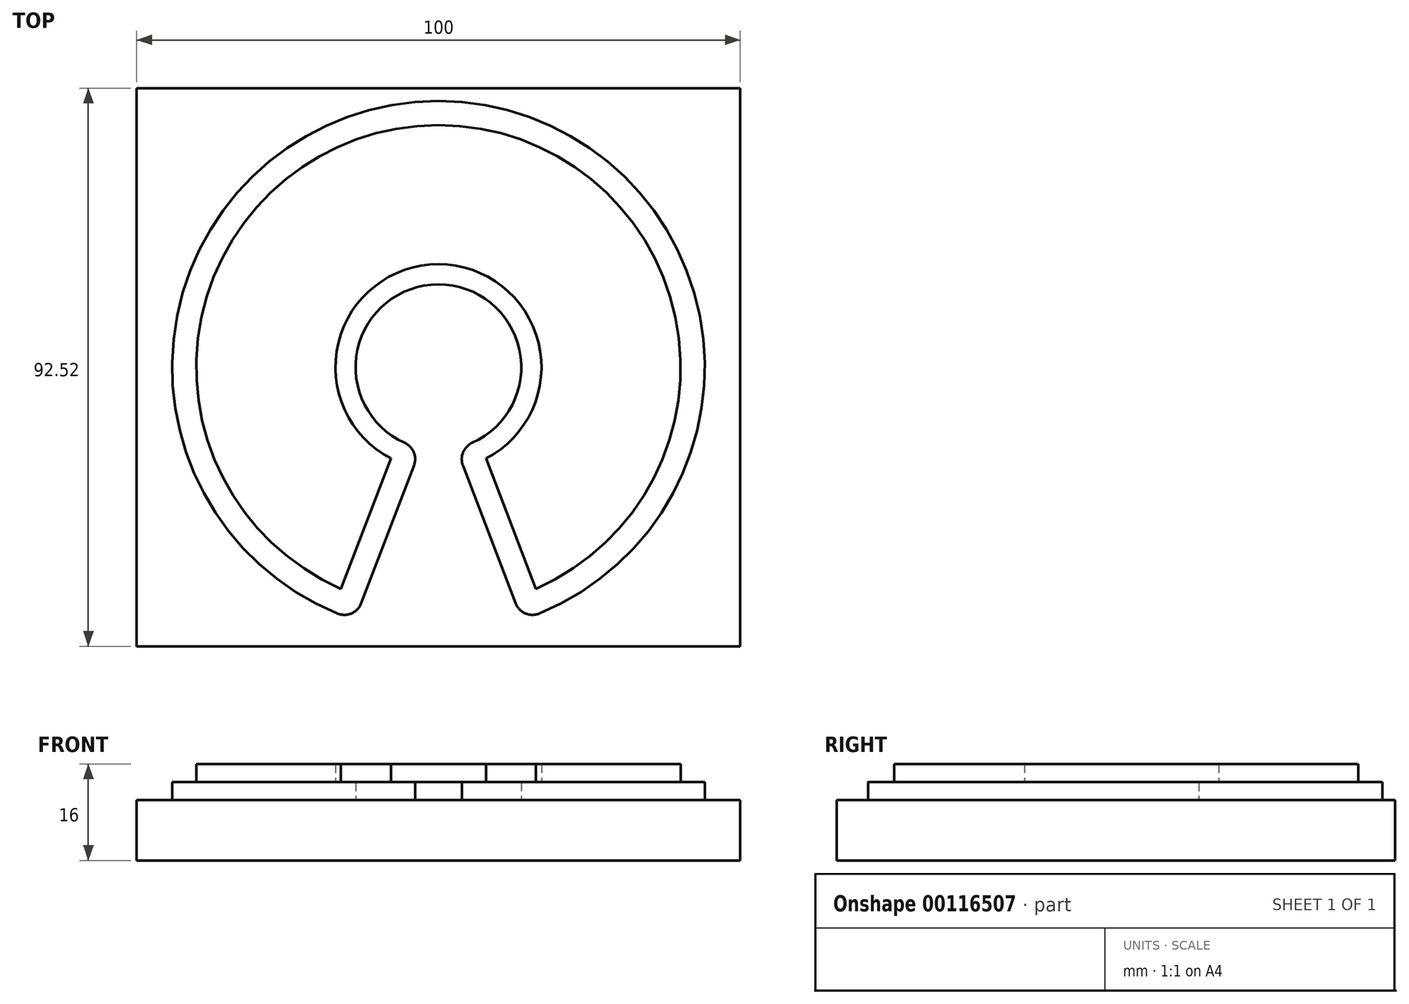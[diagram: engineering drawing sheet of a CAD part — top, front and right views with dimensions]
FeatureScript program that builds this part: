
annotation { "Feature Type Name" : "Feature", "Feature Type Description" : "" }
export const myFeature = defineFeature(function(context is Context, id is Id, definition is map)
    precondition{}
    {
        {
            var Q0;
            Q0=qCreatedBy(makeId("Top.planeOp"),FACE);
            var sketch = newSketch(context, id + "F0", { "sketchPlane" : qUnion([Q0])});
            skLineSegment(sketch, "E0.bottom", {"start": v(50, 46.26) * mm, "end": v(-50, 46.26) * mm});
            skLineSegment(sketch, "E0.top", {"start": v(50, -46.26) * mm, "end": v(-50, -46.26) * mm});
            skLineSegment(sketch, "E0.left", {"start": v(50, 46.26) * mm, "end": v(50, -46.26) * mm});
            skLineSegment(sketch, "E0.right", {"start": v(-50, 46.26) * mm, "end": v(-50, -46.26) * mm});
            skPoint(sketch, "E0.middle", {"position": v(0, 0) * mm});
            skArc(sketch, "E1", {"start": v(16.16, -36.73) * mm, "mid": v(0, 40.13) * mm, "end": v(-16.16, -36.73) * mm});
            skArc(sketch, "E2.0", {"start": v(13.85, -41.9) * mm, "mid": v(0, 44.13) * mm, "end": v(-13.85, -41.9) * mm});
            skArc(sketch, "E3", {"start": v(2.94, -13.41) * mm, "mid": v(0, 13.73) * mm, "end": v(-2.94, -13.41) * mm});
            skLineSegment(sketch, "E4", {"start": v(-7.88, -15.14) * mm, "end": v(-16.16, -36.73) * mm});
            skLineSegment(sketch, "E5.0", {"start": v(-2.94, -13.41) * mm, "end": v(-13.85, -41.9) * mm});
            skLineSegment(sketch, "E6", {"start": v(0, 0) * mm, "end": v(0, -52.2) * mm, "construction": true});
            skLineSegment(sketch, "E7.MirrorCS", {"start": v(7.88, -15.14) * mm, "end": v(16.16, -36.73) * mm});
            skLineSegment(sketch, "E8.MirrorCS", {"start": v(2.94, -13.41) * mm, "end": v(13.85, -41.9) * mm});
            skPoint(sketch, "E9.orphan", {"position": v(1.18, -8.84) * mm});
            skPoint(sketch, "E10.orphan", {"position": v(4.9, -7.35) * mm});
            skPoint(sketch, "E11.orphan", {"position": v(-1.18, -8.84) * mm});
            skPoint(sketch, "E12.orphan", {"position": v(-4.9, -7.35) * mm});
            skArc(sketch, "E13.trimOffspring", {"start": v(7.88, -15.14) * mm, "mid": v(0, 17.07) * mm, "end": v(-7.88, -15.14) * mm});
            skPoint(sketch, "E14.trimOffspring.end.orphan", {"position": v(-17.71, -51.97) * mm});
            skPoint(sketch, "E15.orphan", {"position": v(17.71, -51.97) * mm});
            skPoint(sketch, "E16.orphan", {"position": v(21.28, -50.56) * mm});
            skPoint(sketch, "E17.trimOffspring.end.orphan", {"position": v(-21.28, -50.56) * mm});
            skSolve(sketch);
        }
        {
            var Q0;
            Q0 = qSketchRegion(id + "F0", true);
            var Q1;
            Q1=makeQuery(id+"F0.imprint","IMPRINT",FACE,{"disambiguationData":[TD([[makeQuery(id+"F0.imprint","IMPRINT",EDGE,{"derivedFrom":sQuery(id+"F0.wireOp",EDGE,"E1")}),1.0]])]});
            var Q2;
            Q2=makeQuery(id+"F0.imprint","IMPRINT",FACE,{"disambiguationData":[TD([[makeQuery(id+"F0.imprint","IMPRINT",EDGE,{"derivedFrom":sQuery(id+"F0.wireOp",EDGE,"E1")}),-1.0]])]});
            extrude(context, id + "F1", {"entities" : qUnion([Q0, Q1, Q2]), "oppositeDirection" : true, "depth" : 10 * mm});
        }
        {
            var Q0;
            Q0=makeQuery(id+"F0.imprint","IMPRINT",FACE,{"disambiguationData":[TD([[makeQuery(id+"F0.imprint","IMPRINT",EDGE,{"derivedFrom":sQuery(id+"F0.wireOp",EDGE,"E1")}),-1.0]])]});
            var Q1;
            Q1=makeQuery(id+"F0.imprint","IMPRINT",FACE,{"disambiguationData":[TD([[makeQuery(id+"F0.imprint","IMPRINT",EDGE,{"derivedFrom":sQuery(id+"F0.wireOp",EDGE,"E1")}),1.0]])]});
            extrude(context, id + "F2", {"entities" : qUnion([Q0, Q1]), "operationType" : NewBodyOperationType.ADD, "depth" : 3 * mm});
        }
        {
            var Q0;
            Q0=makeQuery(id+"F0.imprint","IMPRINT",FACE,{"disambiguationData":[TD([[makeQuery(id+"F0.imprint","IMPRINT",EDGE,{"derivedFrom":sQuery(id+"F0.wireOp",EDGE,"E1")}),1.0]])]});
            extrude(context, id + "F3", {"entities" : qUnion([Q0]), "operationType" : NewBodyOperationType.ADD, "depth" : 6 * mm});
        }
        {
            var Q0;
            Q0=makeQuery(id+"F2.opExtrude","SWEPT_EDGE",EDGE,{"disambiguationData":[OSD([sQuery(id+"F0.wireOp",EDGE,"E3"),sQuery(id+"F0.wireOp",EDGE,"E5.0")])]});
            var Q1;
            Q1=makeQuery(id+"F2.opExtrude","SWEPT_EDGE",EDGE,{"disambiguationData":[OSD([sQuery(id+"F0.wireOp",EDGE,"E3"),sQuery(id+"F0.wireOp",EDGE,"E8.MirrorCS")])]});
            var Q2;
            Q2=makeQuery(id+"F2.opExtrude","SWEPT_EDGE",EDGE,{"disambiguationData":[OSD([sQuery(id+"F0.wireOp",EDGE,"E2.0"),sQuery(id+"F0.wireOp",EDGE,"E8.MirrorCS")])]});
            var Q3;
            Q3=makeQuery(id+"F2.opExtrude","SWEPT_EDGE",EDGE,{"disambiguationData":[OSD([sQuery(id+"F0.wireOp",EDGE,"E2.0"),sQuery(id+"F0.wireOp",EDGE,"E5.0")])]});
            fillet(context, id + "F4", {"entities" : qUnion([Q0, Q1, Q2, Q3]), "radius" : 3 * mm, "tangentPropagation" : true, "allowEdgeOverflow" : false});
        }
    });
